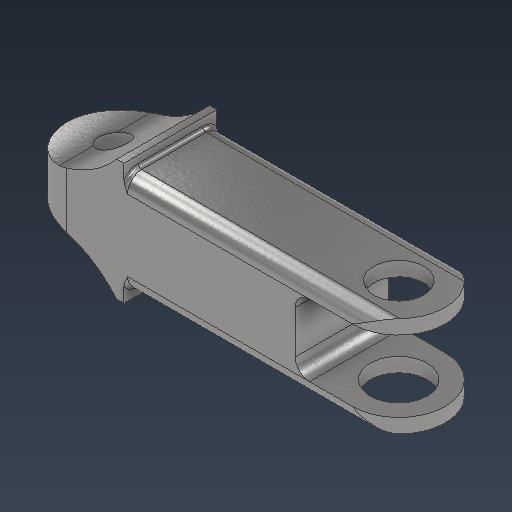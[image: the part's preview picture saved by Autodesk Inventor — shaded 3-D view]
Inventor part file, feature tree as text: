
AUTODESK INVENTOR PART (.ipt)
format: ipt  version: 2021 (Build 250183000, 183)  size: 304,128 bytes
history: native  units: mm
features: sketch x8, extrude x5, fillet x4, hole x3, other x2, mirror x1, projected_geometry x1
ambient origin geometry x8: Origin, YZ Plane, XZ Plane, XY Plane, X Axis, Y Axis, Z Axis, Center Point
bodies: Solid1 (feature_tree)
feature tree (24):
  extrude  "Extrusion1"  Depth=6.5mm
  sketch  "Sketch2"  dims[d4=40.0mm d5=20.0mm]
  other  "midPlane"
  extrude  "Extrusion4"  Depth=20.0mm
  hole  "Hole2"  [1 undecoded]
  sketch  "Sketch8"  dims[d12=0.0mm d35=14.0mm]
  hole  "Hole3"  [1 undecoded]
  hole  "Hole4"  [1 undecoded]
  fillet  "Fillet3"  Radius=8.0mm
  extrude  "Extrusion7"  TaperAngle=0.0deg  [1 undecoded]
  extrude  "Extrusion8"  Depth=0.5mm
  extrude  "Extrusion9"  Depth=0.5mm
  other  "lateralPlane"
  fillet  "Fillet6"  Radius=1.0mm
  mirror  "Mirror1"
  fillet  "Fillet8"  Radius=1.5mm
  fillet  "Fillet7"  Radius=1.5mm
  sketch  "Sketch1"  dims[d0=13.0mm d2=6.5mm]
  sketch  "Sketch5"  dims[d6=14.0mm d7=0.0mm d9=0.0mm]
  sketch  "Sketch9"  dims[d36=10.0mm d37=2.0mm d38=8.0mm]
  sketch  "Sketch10"  dims[d39=20.0mm d40=0.0mm d41=0.0mm]
  sketch  "Sketch11"  dims[d42=5.0mm d43=6.0mm d44=7.0mm d45=2.0mm d46=90.0deg d47=8.0mm d48=0.0mm]
  projected_geometry  "Projected Loop1"
  sketch  "Sketch12"  dims[d55=6.0mm d56=6.0mm d57=8.0mm d58=2.0mm d59=90.0deg d60=8.0mm d61=0.0mm d62=4.0mm d63=6.0mm d64=8.0mm d65=2.0mm d66=90.0deg d67=8.0mm d68=0.0mm d69=2.0mm d70=7.0mm d71=1.0mm d72=1.5mm d73=0.0mm d75=1.5mm d76=0.0mm d78=25.0mm d79=14.0mm d80=25.0mm d81=6.0mm d82=4.0mm d83=0.0mm d84=0.0mm d85=15.0mm d86=0.5mm d87=2.0mm]
note: 4 required parameter values undecoded (feature->parameter linkage not recoverable at this tier; creation-order binding heuristic only, values carry confidence <= 0.55)
